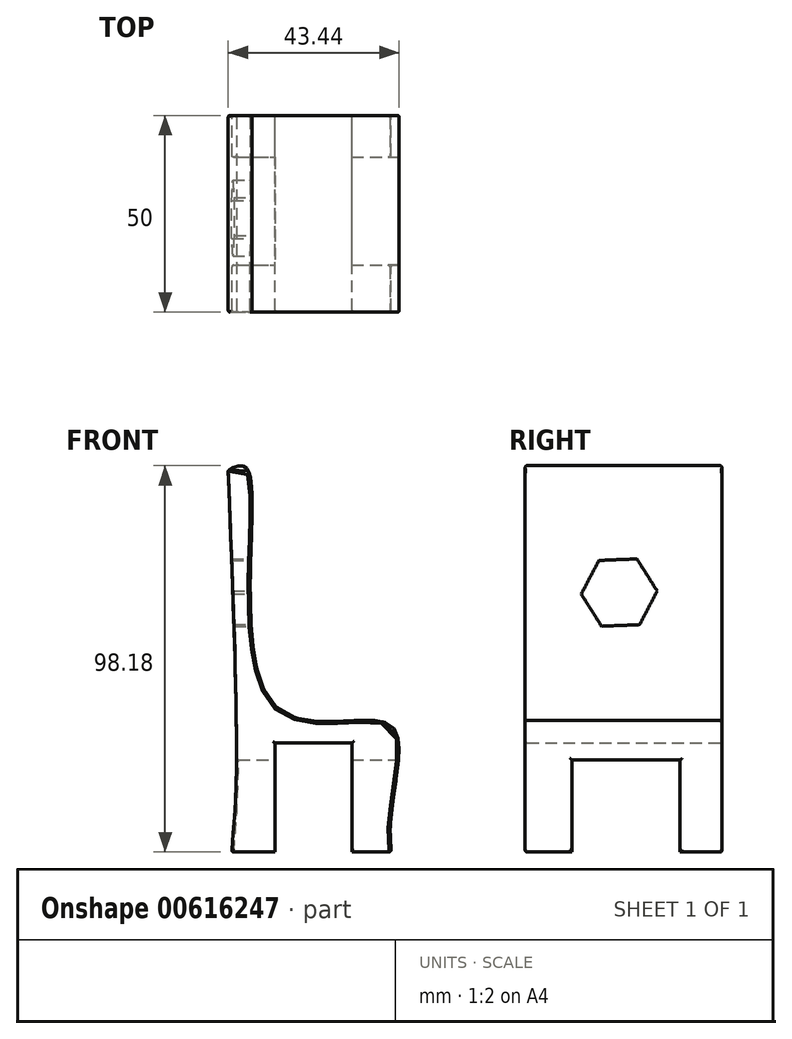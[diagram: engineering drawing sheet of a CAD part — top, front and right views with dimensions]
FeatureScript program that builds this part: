
annotation { "Feature Type Name" : "Feature", "Feature Type Description" : "" }
export const myFeature = defineFeature(function(context is Context, id is Id, definition is map)
    precondition{}
    {
        {
            var Q0;
            Q0=qCreatedBy(makeId("Front.planeOp"),FACE);
            var sketch = newSketch(context, id + "F0", { "sketchPlane" : qUnion([Q0])});
            skFitSpline(sketch, "E0", {"points": [v(-38.38, 45.78) * mm, v(-36.3, -30.67) * mm, v(-37.49, -51.22) * mm], "startDerivative": vector(5.33, -134.63) * mm, "endDerivative": vector(-4.6, -50.99) * mm});
            skLineSegment(sketch, "E1", {"start": v(-37.49, -51.22) * mm, "end": v(-26.52, -51.22) * mm});
            skLineSegment(sketch, "E2", {"start": v(-26.52, -51.22) * mm, "end": v(-26.52, -23.53) * mm});
            skLineSegment(sketch, "E3", {"start": v(-26.52, -23.53) * mm, "end": v(-6.94, -23.53) * mm});
            skLineSegment(sketch, "E4", {"start": v(-6.94, -23.53) * mm, "end": v(-6.94, -51.22) * mm});
            skLineSegment(sketch, "E5", {"start": v(-6.94, -51.22) * mm, "end": v(3.02, -51.22) * mm});
            skFitSpline(sketch, "E6", {"points": [v(3.02, -51.22) * mm, v(3.02, -19.09) * mm, v(-26.82, -13.75) * mm, v(-33.34, 45.87) * mm, v(-38.38, 45.78) * mm], "startDerivative": vector(-19.12, 139.1) * mm, "endDerivative": vector(-56.6, -28.43) * mm});
            skSolve(sketch);
        }
        {
            var Q0;
            Q0 = qSketchRegion(id + "F0", true);
            extrude(context, id + "F1", {"entities" : qUnion([Q0]), "depth" : 50 * mm, "offsetDistance" : 25.4 * mm});
        }
        {
            var Q0;
            Q0=qCreatedBy(makeId("Right.planeOp"),FACE);
            var sketch = newSketch(context, id + "F2", { "sketchPlane" : qUnion([Q0])});
            skLineSegment(sketch, "E7.bottom", {"start": v(-38.06, -27.85) * mm, "end": v(-10.65, -27.85) * mm});
            skLineSegment(sketch, "E7.top", {"start": v(-38.06, -53.23) * mm, "end": v(-10.65, -53.23) * mm});
            skLineSegment(sketch, "E7.left", {"start": v(-38.06, -27.85) * mm, "end": v(-38.06, -53.23) * mm});
            skLineSegment(sketch, "E7.right", {"start": v(-10.65, -27.85) * mm, "end": v(-10.65, -53.23) * mm});
            skSolve(sketch);
        }
        {
            var Q0;
            Q0 = qSketchRegion(id + "F2", true);
            extrude(context, id + "F3", {"entities" : qUnion([Q0]), "operationType" : NewBodyOperationType.REMOVE, "endBound" : BoundingType.THROUGH_ALL, "oppositeDirection" : true, "depth" : 25 * mm, "offsetDistance" : 25 * mm, "hasSecondDirection" : true, "secondDirectionOppositeDirection" : false, "secondDirectionDepth" : 25 * mm});
        }
        {
            var Q0;
            Q0=makeQuery(id+"F1.opExtrude","SWEPT_FACE",FACE,{"disambiguationData":[OSD([sQuery(id+"F0.wireOp",EDGE,"E0")])]});
            fillet(context, id + "F4", {"entities" : qUnion([Q0]), "radius" : 0.5 * mm, "tangentPropagation" : true, "allowEdgeOverflow" : false});
        }
        {
            var Q0;
            Q0=makeQuery(id+"F1.opExtrude","CAP_FACE",FACE,{"disambiguationData":[OSD([sQuery(id+"F0.wireOp",EDGE,"E0"),sQuery(id+"F0.wireOp",EDGE,"E1"),sQuery(id+"F0.wireOp",EDGE,"E2"),sQuery(id+"F0.wireOp",EDGE,"E3"),sQuery(id+"F0.wireOp",EDGE,"E4"),sQuery(id+"F0.wireOp",EDGE,"E5"),sQuery(id+"F0.wireOp",EDGE,"E6")])],"isStart":true});
            fillet(context, id + "F5", {"entities" : qUnion([Q0]), "radius" : 0.5 * mm, "tangentPropagation" : true, "allowEdgeOverflow" : false});
        }
        {
            var Q0;
            Q0=makeQuery(id+"F1.opExtrude","CAP_FACE",FACE,{"disambiguationData":[OSD([sQuery(id+"F0.wireOp",EDGE,"E0"),sQuery(id+"F0.wireOp",EDGE,"E1"),sQuery(id+"F0.wireOp",EDGE,"E2"),sQuery(id+"F0.wireOp",EDGE,"E3"),sQuery(id+"F0.wireOp",EDGE,"E4"),sQuery(id+"F0.wireOp",EDGE,"E5"),sQuery(id+"F0.wireOp",EDGE,"E6")])],"isStart":false});
            fillet(context, id + "F6", {"entities" : qUnion([Q0]), "radius" : 0.5 * mm, "tangentPropagation" : true, "allowEdgeOverflow" : false});
        }
        {
            var Q0;
            Q0=makeQuery(id+"F1.opExtrude","SWEPT_FACE",FACE,{"disambiguationData":[OSD([sQuery(id+"F0.wireOp",EDGE,"E6")])]});
            fillet(context, id + "F7", {"entities" : qUnion([Q0]), "radius" : 0.5 * mm, "tangentPropagation" : true, "allowEdgeOverflow" : false});
        }
        {
            var Q0;
            Q0=qCreatedBy(makeId("Right.planeOp"),FACE);
            var sketch = newSketch(context, id + "F8", { "sketchPlane" : qUnion([Q0])});
            skCircle(sketch, "E8.cCircle", {"center": v(-26.1, 14.73) * mm, "radius": 8.36 * mm, "construction": true});
            skLineSegment(sketch, "E8.0", {"start": v(-20.94, 6.57) * mm, "end": v(-30.59, 6.18) * mm});
            skLineSegment(sketch, "E8.1", {"start": v(-30.59, 6.18) * mm, "end": v(-35.75, 14.34) * mm});
            skLineSegment(sketch, "E8.2", {"start": v(-35.75, 14.34) * mm, "end": v(-31.27, 22.89) * mm});
            skLineSegment(sketch, "E8.3", {"start": v(-31.27, 22.89) * mm, "end": v(-21.62, 23.28) * mm});
            skLineSegment(sketch, "E8.4", {"start": v(-21.62, 23.28) * mm, "end": v(-16.46, 15.12) * mm});
            skLineSegment(sketch, "E8.5", {"start": v(-16.46, 15.12) * mm, "end": v(-20.94, 6.57) * mm});
            skPoint(sketch, "E8.0.midPoint", {"position": v(-25.77, 6.37) * mm});
            skSolve(sketch);
        }
        {
            var Q0;
            Q0 = qSketchRegion(id + "F8", true);
            extrude(context, id + "F9", {"entities" : qUnion([Q0]), "operationType" : NewBodyOperationType.REMOVE, "oppositeDirection" : true, "depth" : 56.6 * mm, "offsetDistance" : 25 * mm});
        }
    });
